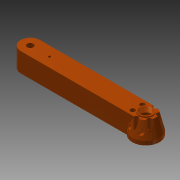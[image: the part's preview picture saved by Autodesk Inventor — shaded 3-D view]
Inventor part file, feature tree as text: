
AUTODESK INVENTOR PART (.ipt)
format: ipt  version: 2013 (Build 170138000, 138)  size: 315,904 bytes
history: native  units: mm
features: sketch x14, extrude x12, projected_geometry x4, revolve x1, pattern_circular x1, helix x1
ambient origin geometry x8: Origin, YZ Plane, XZ Plane, XY Plane, X Axis, Y Axis, Z Axis, Center Point
bodies: Solid1 (feature_tree)
feature tree (33):
  extrude  "Extrusion1"  Depth=8.1mm
  extrude  "Extrusion5"  Depth=16.2mm
  extrude  "Extrusion16"  Depth=25.0mm
  extrude  "Extrusion24"  Depth=10.0mm TaperAngle=0.0deg
  revolve  "Revolution1"  [1 undecoded]
  extrude  "Extrusion25"  Depth=5.0mm
  extrude  "Extrusion26"  TaperAngle=90.0deg  [1 undecoded]
  pattern_circular  "Circular Pattern1"  Count=2  [1 undecoded]
  extrude  "Extrusion27"  Depth=20.0mm TaperAngle=0.0deg
  extrude  "Extrusion28"  Depth=14.5mm
  extrude  "Extrusion29"  Depth=20.0mm TaperAngle=0.0deg
  extrude  "Extrusion30"  Depth=20.0mm TaperAngle=0.0deg
  extrude  "Extrusion31"  Depth=5.6mm
  extrude  "Extrusion32"  Depth=2.5mm TaperAngle=0.0deg
  helix  "Coil3"  [1 undecoded]
  sketch  "Sketch1"  dims[d0=12.5mm d3=8.1mm]
  sketch  "Sketch5"  dims[d4=25.0mm d5=0.0mm d19=16.2mm]
  sketch  "Sketch17"  dims[d21=19.0mm d22=0.0mm d85=25.0mm]
  sketch  "Sketch26"  dims[d86=3.0mm d87=10.0mm d88=0.0mm]
  sketch  "Sketch27"  dims[d121=150.0mm d122=18.0mm]
  sketch  "Sketch28"  dims[d125=1.5mm d126=0.0mm d127=5.0mm]
  sketch  "Sketch29"  dims[d129=5.0mm d130=90.0deg]
  sketch  "Sketch30"  dims[d131=30.0deg]
  sketch  "Sketch31"  dims[d132=12.5mm]
  sketch  "Sketch32"  dims[d134=6.0mm d135=20.0mm d136=0.0mm]
  sketch  "Sketch33"  dims[d137=3.2mm d139=20.0mm d140=0.0mm]
  projected_geometry  "Projected Loop4"
  sketch  "Sketch34"  dims[d141=60.0mm d142=360.0deg d144=14.5mm]
  sketch  "Sketch35"  dims[d146=6.0mm d147=20.0mm d148=0.0mm]
  sketch  "Sketch36"  dims[d149=3.2mm d151=20.0mm d152=0.0mm d153=5.6mm d154=2.5mm d155=25.0mm d156=0.0mm d157=0.0mm d158=2.5mm d159=0.0mm d160=13.9mm d162=2.5mm d163=0.0mm d164=2.5mm d165=-7.853982mm d166=2.0mm d167=2.0001mm d168=10.0mm d169=100.0mm d170=0.0mm d171=90.0deg d172=90.0deg d173=0.0mm d174=0.0mm]
  projected_geometry  "Project Cut Edges3"
  projected_geometry  "Project Cut Edges4"
  projected_geometry  "Project Cut Edges5"
note: 4 required parameter values undecoded (feature->parameter linkage not recoverable at this tier; creation-order binding heuristic only, values carry confidence <= 0.55)